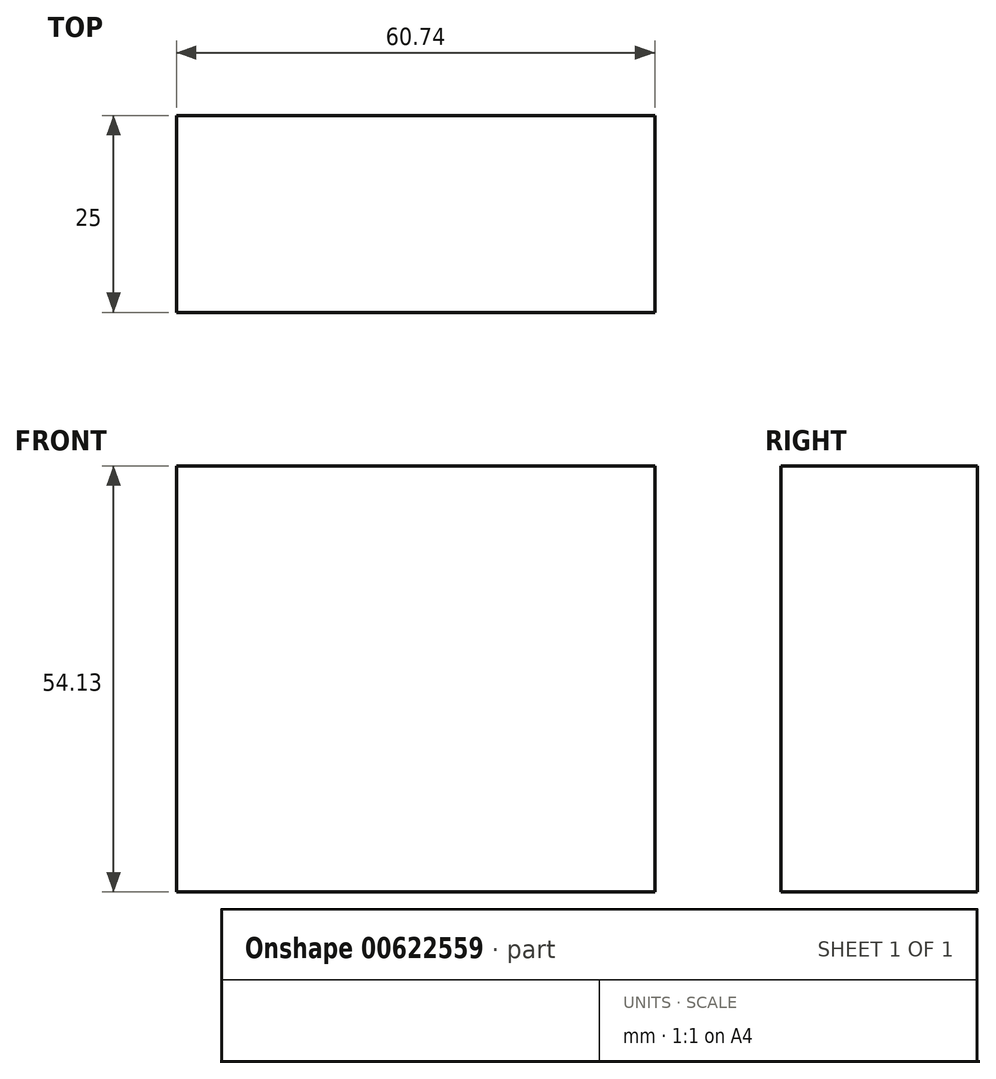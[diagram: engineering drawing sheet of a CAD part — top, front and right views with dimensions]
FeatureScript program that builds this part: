
annotation { "Feature Type Name" : "Feature", "Feature Type Description" : "" }
export const myFeature = defineFeature(function(context is Context, id is Id, definition is map)
    precondition{}
    {
        {
            var Q0;
            Q0=qCreatedBy(makeId("Front.planeOp"),FACE);
            var sketch = newSketch(context, id + "F0", { "sketchPlane" : qUnion([Q0])});
            skLineSegment(sketch, "E0.bottom", {"start": v(-122.12, 54.13) * mm, "end": v(-61.38, 54.13) * mm});
            skLineSegment(sketch, "E0.top", {"start": v(-122.12, 0) * mm, "end": v(-61.38, 0) * mm});
            skLineSegment(sketch, "E0.left", {"start": v(-122.12, 54.13) * mm, "end": v(-122.12, 0) * mm});
            skLineSegment(sketch, "E0.right", {"start": v(-61.38, 54.13) * mm, "end": v(-61.38, 0) * mm});
            skSolve(sketch);
        }
        {
            var Q0;
            Q0 = qSketchRegion(id + "F0", true);
            extrude(context, id + "F1", {"entities" : qUnion([Q0]), "depth" : 25 * mm, "offsetDistance" : 25 * mm});
        }
    });
